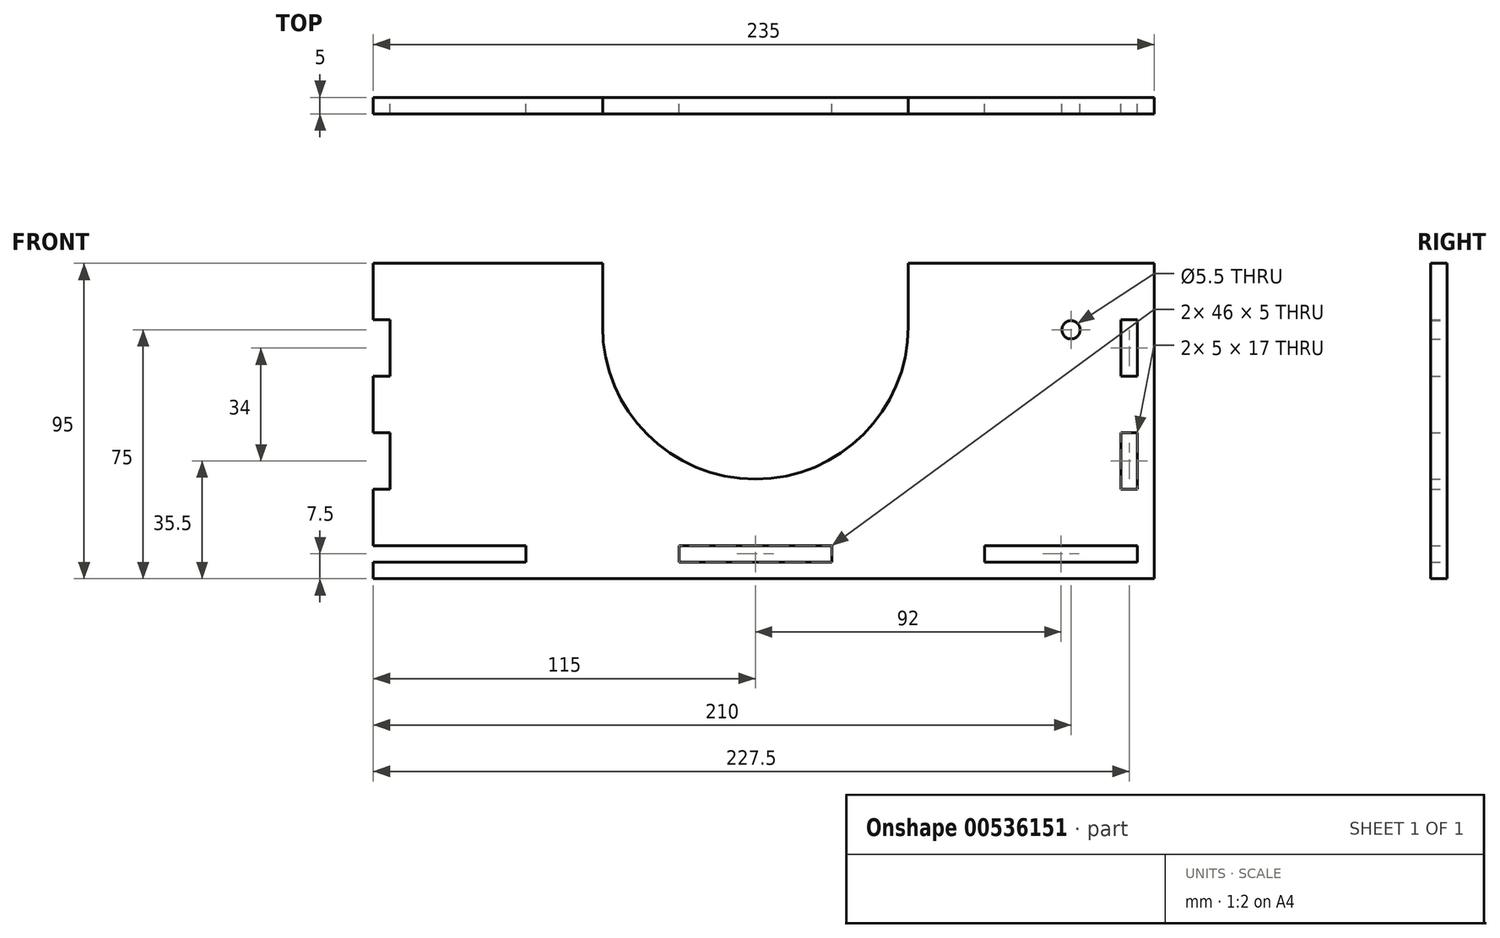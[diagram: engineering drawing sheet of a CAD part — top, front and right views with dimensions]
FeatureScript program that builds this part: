
annotation { "Feature Type Name" : "Feature", "Feature Type Description" : "" }
export const myFeature = defineFeature(function(context is Context, id is Id, definition is map)
    precondition{}
    {
        {
            var Q0;
            Q0=qCreatedBy(makeId("Front.planeOp"),FACE);
            var sketch = newSketch(context, id + "F0", { "sketchPlane" : qUnion([Q0])});
            skLineSegment(sketch, "E0.bottom", {"start": v(110, 42.5) * mm, "end": v(46, 42.5) * mm});
            skLineSegment(sketch, "E0.right", {"start": v(-110, 25.5) * mm, "end": v(-110, 8.5) * mm});
            skPoint(sketch, "E0.middle", {"position": v(0, 0) * mm});
            skLineSegment(sketch, "E1", {"start": v(-115, 42.5) * mm, "end": v(-115, -42.5) * mm, "construction": true});
            skLineSegment(sketch, "E2", {"start": v(-115, -47.5) * mm, "end": v(-69, -47.5) * mm, "construction": true});
            skLineSegment(sketch, "E3", {"start": v(115, -25.5) * mm, "end": v(115, -8.5) * mm, "construction": true});
            skArc(sketch, "E4", {"start": v(-46, 23.5) * mm, "mid": v(0, -22.5) * mm, "end": v(46, 23.5) * mm});
            skLineSegment(sketch, "E5.trimOffspring", {"start": v(-46, 42.5) * mm, "end": v(-110, 42.5) * mm});
            skLineSegment(sketch, "E6", {"start": v(-46, 23.5) * mm, "end": v(-46, 42.5) * mm});
            skLineSegment(sketch, "E7", {"start": v(46, 23.5) * mm, "end": v(46, 42.5) * mm});
            skLineSegment(sketch, "E8", {"start": v(-110, 42.5) * mm, "end": v(-115, 42.5) * mm});
            skLineSegment(sketch, "E9", {"start": v(-115, 25.5) * mm, "end": v(-110, 25.5) * mm});
            skLineSegment(sketch, "E10", {"start": v(-110, 8.5) * mm, "end": v(-115, 8.5) * mm});
            skLineSegment(sketch, "E11", {"start": v(-115, 8.5) * mm, "end": v(-115, -8.5) * mm});
            skLineSegment(sketch, "E12", {"start": v(-115, -8.5) * mm, "end": v(-110, -8.5) * mm});
            skLineSegment(sketch, "E13", {"start": v(-110, -8.5) * mm, "end": v(-110, -25.5) * mm});
            skLineSegment(sketch, "E14", {"start": v(-110, -25.5) * mm, "end": v(-115, -25.5) * mm});
            skLineSegment(sketch, "E15", {"start": v(-115, -25.5) * mm, "end": v(-115, -42.5) * mm});
            skLineSegment(sketch, "E16", {"start": v(-115, 42.5) * mm, "end": v(-115, 25.5) * mm});
            skLineSegment(sketch, "E17.MirrorCS", {"start": v(110, 42.5) * mm, "end": v(115, 42.5) * mm});
            skLineSegment(sketch, "E18.MirrorCS", {"start": v(115, -8.5) * mm, "end": v(110, -8.5) * mm});
            skLineSegment(sketch, "E19.MirrorCS", {"start": v(110, -25.5) * mm, "end": v(115, -25.5) * mm});
            skLineSegment(sketch, "E20.trimOffspring", {"start": v(110, -8.5) * mm, "end": v(110, -25.5) * mm});
            skLineSegment(sketch, "E21", {"start": v(-69, -42.5) * mm, "end": v(-69, -47.5) * mm});
            skLineSegment(sketch, "E22", {"start": v(-115, -47.5) * mm, "end": v(-69, -47.5) * mm});
            skLineSegment(sketch, "E23", {"start": v(-23, -42.5) * mm, "end": v(-23, -47.5) * mm});
            skLineSegment(sketch, "E24", {"start": v(-23, -47.5) * mm, "end": v(23, -47.5) * mm});
            skLineSegment(sketch, "E25", {"start": v(23, -47.5) * mm, "end": v(23, -42.5) * mm});
            skLineSegment(sketch, "E26", {"start": v(69, -42.5) * mm, "end": v(69, -47.5) * mm});
            skLineSegment(sketch, "E27", {"start": v(69, -47.5) * mm, "end": v(115, -47.5) * mm});
            skPoint(sketch, "E28.end.orphan", {"position": v(-110, -42.5) * mm});
            skPoint(sketch, "E29.end.orphan", {"position": v(110, -42.5) * mm});
            skLineSegment(sketch, "E30.top", {"start": v(-115, -52.5) * mm, "end": v(115, -52.5) * mm});
            skLineSegment(sketch, "E30.left", {"start": v(-115, -47.5) * mm, "end": v(-115, -52.5) * mm});
            skLineSegment(sketch, "E31", {"start": v(-115, -42.5) * mm, "end": v(-69, -42.5) * mm});
            skLineSegment(sketch, "E32.trimOffspring", {"start": v(-23, -47.5) * mm, "end": v(23, -47.5) * mm, "construction": true});
            skLineSegment(sketch, "E33.trimOffspring", {"start": v(69, -47.5) * mm, "end": v(115, -47.5) * mm, "construction": true});
            skLineSegment(sketch, "E34", {"start": v(-23, -42.5) * mm, "end": v(23, -42.5) * mm});
            skLineSegment(sketch, "E35", {"start": v(69, -42.5) * mm, "end": v(115, -42.5) * mm});
            skLineSegment(sketch, "E36.bottom", {"start": v(115, 42.5) * mm, "end": v(120, 42.5) * mm});
            skLineSegment(sketch, "E36.top", {"start": v(115, -52.5) * mm, "end": v(120, -52.5) * mm});
            skLineSegment(sketch, "E36.right", {"start": v(120, 42.5) * mm, "end": v(120, -52.5) * mm});
            skLineSegment(sketch, "E37.trimOffspring", {"start": v(115, -42.5) * mm, "end": v(115, -47.5) * mm});
            skLineSegment(sketch, "E38.trimOffspring", {"start": v(115, -8.5) * mm, "end": v(115, -25.5) * mm, "construction": true});
            skLineSegment(sketch, "E39.trimOffspring", {"start": v(115, -8.5) * mm, "end": v(115, -25.5) * mm});
            skLineSegment(sketch, "E40.MirrorCS", {"start": v(110, 8.5) * mm, "end": v(115, 8.5) * mm});
            skLineSegment(sketch, "E41.MirrorCS", {"start": v(110, 25.5) * mm, "end": v(110, 8.5) * mm});
            skLineSegment(sketch, "E42.MirrorCS", {"start": v(115, 25.5) * mm, "end": v(110, 25.5) * mm});
            skLineSegment(sketch, "E43", {"start": v(115, 25.5) * mm, "end": v(115, 8.5) * mm});
            skCircle(sketch, "E44", {"center": v(95, 22.5) * mm, "radius": 2.75 * mm});
            skSolve(sketch);
        }
        {
            var Q0;
            Q0 = qSketchRegion(id + "F0", true);
            extrude(context, id + "F1", {"entities" : qUnion([Q0]), "depth" : 5 * mm, "offsetDistance" : 25 * mm});
        }
    });
